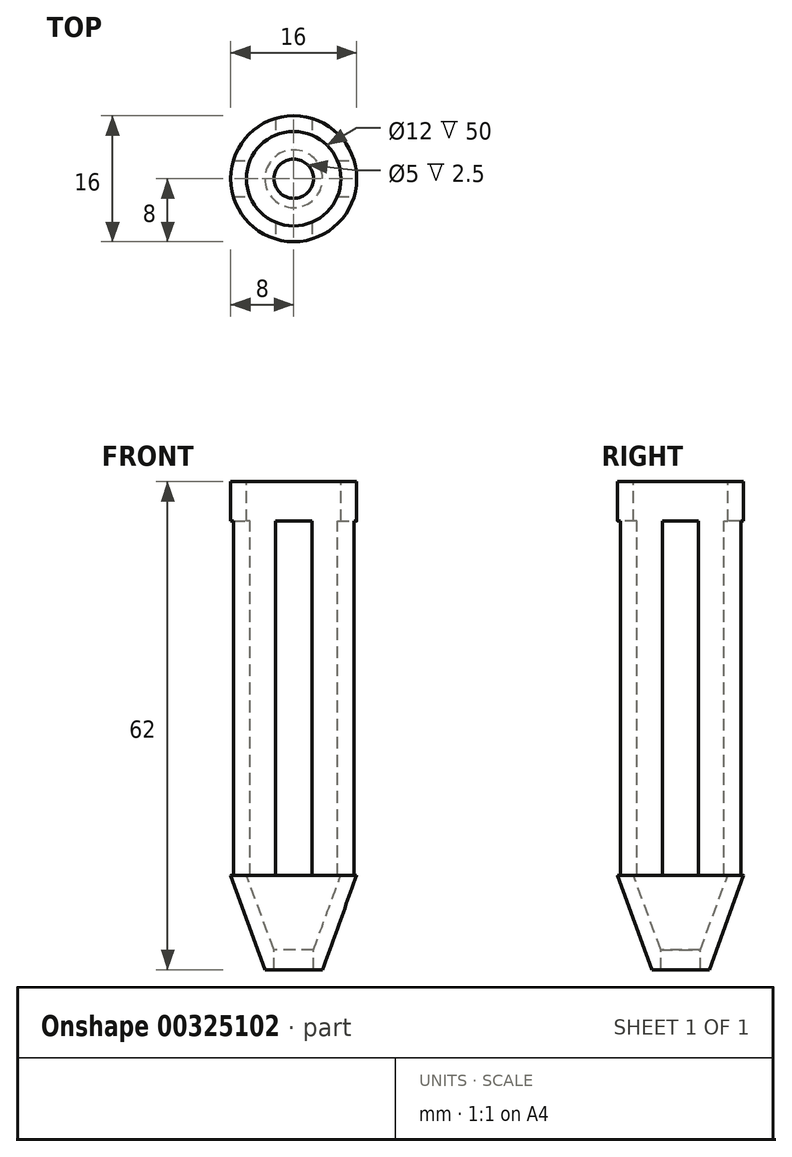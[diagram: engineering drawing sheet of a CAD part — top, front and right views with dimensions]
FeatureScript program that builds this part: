
annotation { "Feature Type Name" : "Feature", "Feature Type Description" : "" }
export const myFeature = defineFeature(function(context is Context, id is Id, definition is map)
    precondition{}
    {
        {
            var Q0;
            Q0=qCreatedBy(makeId("Right.planeOp"),FACE);
            var sketch = newSketch(context, id + "F0", { "sketchPlane" : qUnion([Q0])});
            skLineSegment(sketch, "E0.left", {"start": v(-6, 50) * mm, "end": v(-6, 0) * mm});
            skLineSegment(sketch, "E1", {"start": v(0, 62.99) * mm, "end": v(0, -53) * mm, "construction": true});
            skLineSegment(sketch, "E2.0", {"start": v(-8, 50) * mm, "end": v(-8, 0.02) * mm});
            skLineSegment(sketch, "E3", {"start": v(-8, 50) * mm, "end": v(-6, 50) * mm});
            skLineSegment(sketch, "E4", {"start": v(-6, 0) * mm, "end": v(-2.5, -9.5) * mm});
            skLineSegment(sketch, "E5", {"start": v(-3.66, -12) * mm, "end": v(-2.5, -12) * mm});
            skLineSegment(sketch, "E6", {"start": v(-2.5, -9.5) * mm, "end": v(-2.5, -12) * mm});
            skLineSegment(sketch, "E7", {"start": v(-8, 0.02) * mm, "end": v(-3.66, -12) * mm});
            skSolve(sketch);
        }
        {
            var Q0;
            Q0 = qSketchRegion(id + "F0", true);
            var Q1;
            Q1=sQuery(id+"F0.wireOp",EDGE,"E1");
            revolve(context, id + "F1", {"entities" : qUnion([Q0]), "axis" : qUnion([Q1]), "revolveType" : RevolveType.FULL});
        }
        {
            var Q0;
            Q0=qCreatedBy(makeId("Front.planeOp"),FACE);
            var sketch = newSketch(context, id + "F2", { "sketchPlane" : qUnion([Q0])});
            skLineSegment(sketch, "E8.bottom", {"start": v(-2.3, 45) * mm, "end": v(2.3, 45) * mm});
            skLineSegment(sketch, "E8.top", {"start": v(-2.3, 0) * mm, "end": v(2.3, 0) * mm});
            skLineSegment(sketch, "E8.left", {"start": v(-2.3, 45) * mm, "end": v(-2.3, 0) * mm});
            skLineSegment(sketch, "E8.right", {"start": v(2.3, 45) * mm, "end": v(2.3, 0) * mm});
            skSolve(sketch);
        }
        {
            var Q0;
            Q0 = qSketchRegion(id + "F2", true);
            extrude(context, id + "F3", {"entities" : qUnion([Q0]), "operationType" : NewBodyOperationType.REMOVE, "endBound" : BoundingType.SYMMETRIC, "oppositeDirection" : true, "depth" : 25 * mm});
        }
        {
            var Q0;
            Q0=qCreatedBy(makeId("Right.planeOp"),FACE);
            var sketch = newSketch(context, id + "F4", { "sketchPlane" : qUnion([Q0])});
            skLineSegment(sketch, "E9.bottom", {"start": v(2.3, 0) * mm, "end": v(-2.3, 0) * mm});
            skLineSegment(sketch, "E9.top", {"start": v(2.3, 45) * mm, "end": v(-2.3, 45) * mm});
            skLineSegment(sketch, "E9.left", {"start": v(2.3, 0) * mm, "end": v(2.3, 45) * mm});
            skLineSegment(sketch, "E9.right", {"start": v(-2.3, 0) * mm, "end": v(-2.3, 45) * mm});
            skSolve(sketch);
        }
        {
            var Q0;
            Q0 = qSketchRegion(id + "F4", true);
            extrude(context, id + "F5", {"entities" : qUnion([Q0]), "operationType" : NewBodyOperationType.REMOVE, "endBound" : BoundingType.SYMMETRIC, "oppositeDirection" : true, "depth" : 25 * mm});
        }
    });
